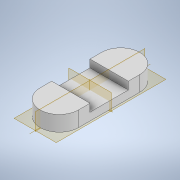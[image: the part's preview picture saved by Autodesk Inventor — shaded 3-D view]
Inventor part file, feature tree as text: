
AUTODESK INVENTOR PART (.ipt)
format: ipt  version: 2022.4 (Build 264492010, 492A)  size: 113,152 bytes
history: native  units: mm
features: extrude x2, sketch x1
ambient origin geometry x8: Origin, YZ Plane, XZ Plane, XY Plane, X Axis, Y Axis, Z Axis, Center Point
bodies: Solid1 (feature_tree)
feature tree (3):
  sketch  "Sketch1"  dims[d0=10.0mm d1=8.0mm d2=3.0mm d3=2.0mm d4=0.0mm d5=4.0mm d6=0.0mm]
  extrude  "Extrusion1"  Depth=8.0mm
  extrude  "Extrusion2"  Depth=4.0mm
